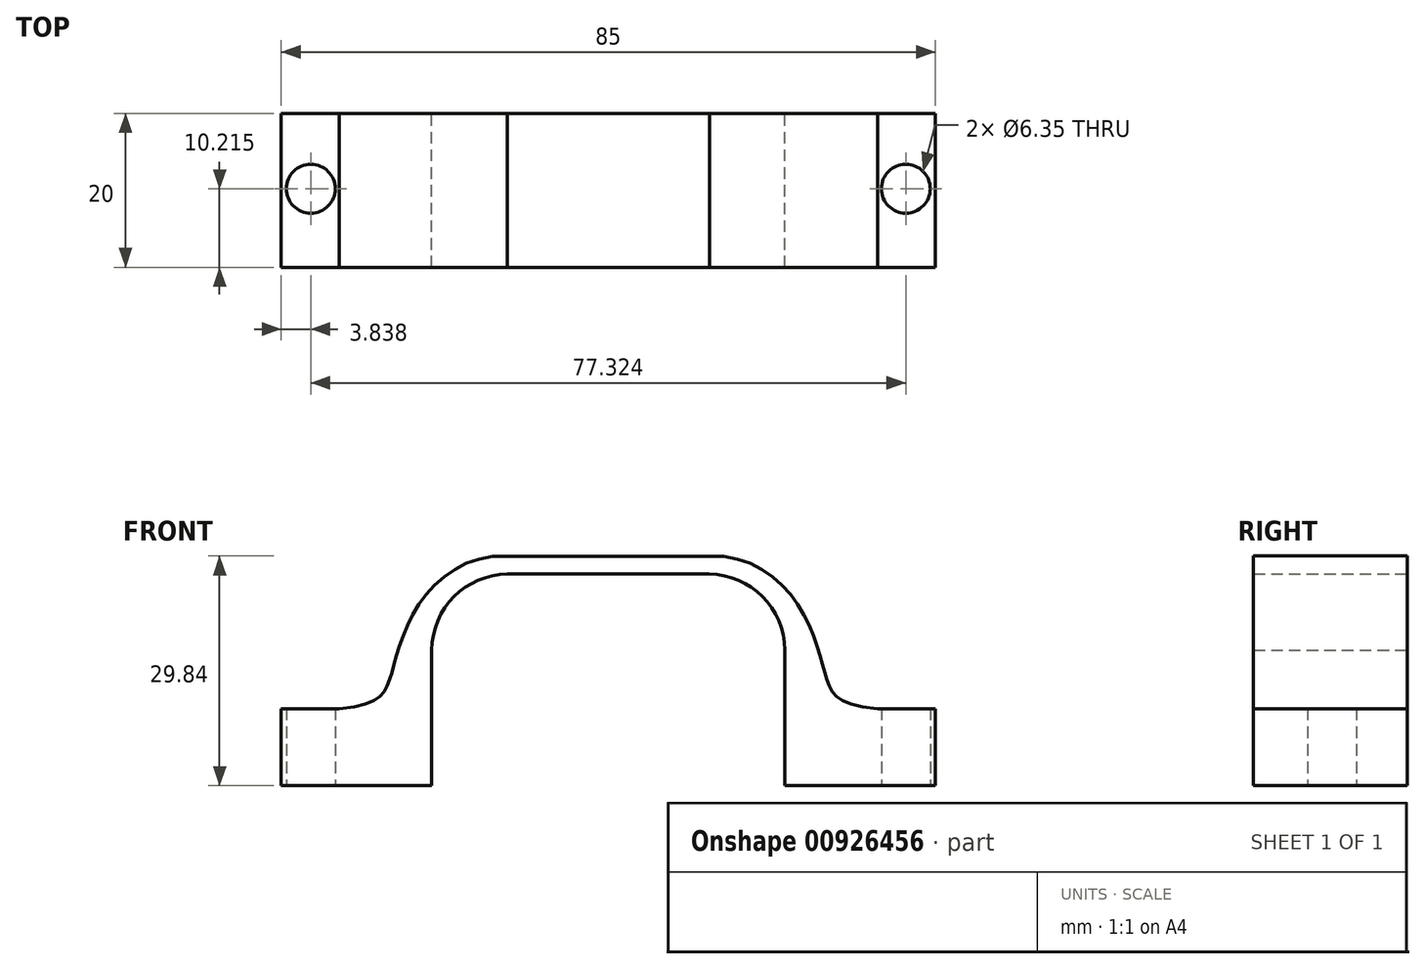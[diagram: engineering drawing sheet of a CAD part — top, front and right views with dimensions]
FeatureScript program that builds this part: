
annotation { "Feature Type Name" : "Feature", "Feature Type Description" : "" }
export const myFeature = defineFeature(function(context is Context, id is Id, definition is map)
    precondition{}
    {
        {
            var Q0;
            Q0=qCreatedBy(makeId("Front.planeOp"),FACE);
            var sketch = newSketch(context, id + "F0", { "sketchPlane" : qUnion([Q0])});
            skLineSegment(sketch, "E0", {"start": v(0, 35.25) * mm, "end": v(0, -18.5) * mm, "construction": true});
            skLineSegment(sketch, "E1", {"start": v(61.88, 0) * mm, "end": v(-65.31, 0) * mm, "construction": true});
            skSolve(sketch);
        }
        {
            var Q0;
            Q0=qCreatedBy(makeId("Top.planeOp"),FACE);
            var sketch = newSketch(context, id + "F1", { "sketchPlane" : qUnion([Q0])});
            skLineSegment(sketch, "E2", {"start": v(0, 27.62) * mm, "end": v(0, -27.15) * mm, "construction": true});
            skSolve(sketch);
        }
        {
            var Q0;
            Q0=qCreatedBy(makeId("Front.planeOp"),FACE);
            var sketch = newSketch(context, id + "F2", { "sketchPlane" : qUnion([Q0])});
            skLineSegment(sketch, "E3.0", {"start": v(-13.13, 29.82) * mm, "end": v(0, 29.82) * mm});
            skLineSegment(sketch, "E4.0", {"start": v(-35, 10) * mm, "end": v(-42.5, 10) * mm});
            skLineSegment(sketch, "E5.0", {"start": v(-42.5, 10) * mm, "end": v(-42.5, 0) * mm});
            skLineSegment(sketch, "E6.0", {"start": v(-22.5, 0) * mm, "end": v(-42.5, 0) * mm});
            skLineSegment(sketch, "E7.0", {"start": v(-22.96, 10) * mm, "end": v(-22.96, 0) * mm});
            skArc(sketch, "E8.0", {"start": v(-22.96, 17.62) * mm, "mid": v(-20.03, 24.57) * mm, "end": v(-13.1, 27.5) * mm});
            skLineSegment(sketch, "E9.0", {"start": v(-13.1, 27.5) * mm, "end": v(0, 27.5) * mm});
            skLineSegment(sketch, "E10.MirrorCS", {"start": v(13.13, 29.82) * mm, "end": v(0, 29.82) * mm});
            skLineSegment(sketch, "E11.MirrorCS", {"start": v(35, 10) * mm, "end": v(42.5, 10) * mm});
            skLineSegment(sketch, "E12.MirrorCS", {"start": v(42.5, 10) * mm, "end": v(42.5, 0) * mm});
            skLineSegment(sketch, "E13.MirrorCS", {"start": v(22.5, 0) * mm, "end": v(42.5, 0) * mm});
            skLineSegment(sketch, "E14.MirrorCS", {"start": v(22.96, 10) * mm, "end": v(22.96, 0) * mm});
            skArc(sketch, "E15.MirrorCS", {"start": v(22.96, 17.62) * mm, "mid": v(20.03, 24.57) * mm, "end": v(13.1, 27.5) * mm});
            skLineSegment(sketch, "E16.MirrorCS", {"start": v(13.1, 27.5) * mm, "end": v(0, 27.5) * mm});
            skLineSegment(sketch, "E17", {"start": v(-22.96, 17.62) * mm, "end": v(-22.96, 10) * mm});
            skLineSegment(sketch, "E18", {"start": v(22.96, 17.62) * mm, "end": v(22.96, 10) * mm});
            skFitSpline(sketch, "E19", {"points": [v(-35, 10) * mm, v(-29, 12.43) * mm, v(-27.69, 16.3) * mm, v(-23.88, 24.6) * mm, v(-13.13, 29.82) * mm], "startDerivative": vector(51.57, 4.91) * mm, "endDerivative": vector(44.51, -2.03) * mm});
            skFitSpline(sketch, "E20.MirrorCS", {"points": [v(35, 10) * mm, v(29, 12.43) * mm, v(27.69, 16.3) * mm, v(23.88, 24.6) * mm, v(13.13, 29.82) * mm], "startDerivative": vector(-51.57, 4.91) * mm, "endDerivative": vector(-44.51, -2.03) * mm});
            skPoint(sketch, "E21", {"position": v(-38.75, 10) * mm});
            skPoint(sketch, "E22", {"position": v(38.75, 10) * mm});
            skSolve(sketch);
        }
        {
            var Q0;
            Q0=makeQuery(id+"F2.imprint","IMPRINT",FACE,{"disambiguationData":[TD([[makeQuery(id+"F2.imprint","IMPRINT",EDGE,{"derivedFrom":sQuery(id+"F2.wireOp",EDGE,"E3.0")}),-1.0]])]});
            extrude(context, id + "F3", {"entities" : qUnion([Q0]), "depth" : 20 * mm, "offsetDistance" : 25.4 * mm});
        }
        {
            var Q0;
            Q0=qCreatedBy(makeId("Top.planeOp"),FACE);
            var sketch = newSketch(context, id + "F4", { "sketchPlane" : qUnion([Q0])});
            skPoint(sketch, "E23", {"position": v(-38.66, -9.79) * mm});
            skPoint(sketch, "E24.MirrorP", {"position": v(38.66, -9.79) * mm});
            skSolve(sketch);
        }
        {
            var Q0;
            Q0=sQuery(id+"F4.wireOp",VERTEX,"E23");
            var Q1;
            Q1=makeQuery(id+"F3.opExtrude","SWEPT_BODY",BODY,{"disambiguationData":[OSD([sQuery(id+"F2.wireOp",EDGE,"E3.0"),sQuery(id+"F2.wireOp",EDGE,"E4.0"),sQuery(id+"F2.wireOp",EDGE,"E5.0"),sQuery(id+"F2.wireOp",EDGE,"E6.0"),sQuery(id+"F2.wireOp",EDGE,"E7.0"),sQuery(id+"F2.wireOp",EDGE,"E8.0"),sQuery(id+"F2.wireOp",EDGE,"E9.0"),sQuery(id+"F2.wireOp",EDGE,"E10.MirrorCS"),sQuery(id+"F2.wireOp",EDGE,"E11.MirrorCS"),sQuery(id+"F2.wireOp",EDGE,"E12.MirrorCS"),sQuery(id+"F2.wireOp",EDGE,"E13.MirrorCS"),sQuery(id+"F2.wireOp",EDGE,"E14.MirrorCS"),sQuery(id+"F2.wireOp",EDGE,"E15.MirrorCS"),sQuery(id+"F2.wireOp",EDGE,"E16.MirrorCS"),sQuery(id+"F2.wireOp",EDGE,"E17"),sQuery(id+"F2.wireOp",EDGE,"E18"),sQuery(id+"F2.wireOp",EDGE,"E19"),sQuery(id+"F2.wireOp",EDGE,"E20.MirrorCS")])]});
            hole(context, id + "F5", {"style" : HoleStyle.SIMPLE, "endStyle" : HoleEndStyle.THROUGH, "oppositeDirection" : true, "holeDiameter" : 6.35 * mm, "majorDiameter" : 6.35 * mm, "isTappedThrough" : true, "tappedDepth" : 12.7 * mm, "tapClearance" : 3, "locations" : qUnion([Q0]), "scope" : qUnion([Q1])});
        }
        {
            var Q0;
            Q0=sQuery(id+"F4.wireOp",VERTEX,"E24.MirrorP");
            var Q1;
            Q1=makeQuery(id+"F3.opExtrude","SWEPT_BODY",BODY,{"disambiguationData":[OSD([sQuery(id+"F2.wireOp",EDGE,"E3.0"),sQuery(id+"F2.wireOp",EDGE,"E4.0"),sQuery(id+"F2.wireOp",EDGE,"E5.0"),sQuery(id+"F2.wireOp",EDGE,"E6.0"),sQuery(id+"F2.wireOp",EDGE,"E7.0"),sQuery(id+"F2.wireOp",EDGE,"E8.0"),sQuery(id+"F2.wireOp",EDGE,"E9.0"),sQuery(id+"F2.wireOp",EDGE,"E10.MirrorCS"),sQuery(id+"F2.wireOp",EDGE,"E11.MirrorCS"),sQuery(id+"F2.wireOp",EDGE,"E12.MirrorCS"),sQuery(id+"F2.wireOp",EDGE,"E13.MirrorCS"),sQuery(id+"F2.wireOp",EDGE,"E14.MirrorCS"),sQuery(id+"F2.wireOp",EDGE,"E15.MirrorCS"),sQuery(id+"F2.wireOp",EDGE,"E16.MirrorCS"),sQuery(id+"F2.wireOp",EDGE,"E17"),sQuery(id+"F2.wireOp",EDGE,"E18"),sQuery(id+"F2.wireOp",EDGE,"E19"),sQuery(id+"F2.wireOp",EDGE,"E20.MirrorCS")])]});
            hole(context, id + "F6", {"style" : HoleStyle.SIMPLE, "endStyle" : HoleEndStyle.THROUGH, "oppositeDirection" : true, "holeDiameter" : 6.35 * mm, "majorDiameter" : 6.35 * mm, "isTappedThrough" : true, "tappedDepth" : 12.7 * mm, "tapClearance" : 3, "locations" : qUnion([Q0]), "scope" : qUnion([Q1])});
        }
    });
